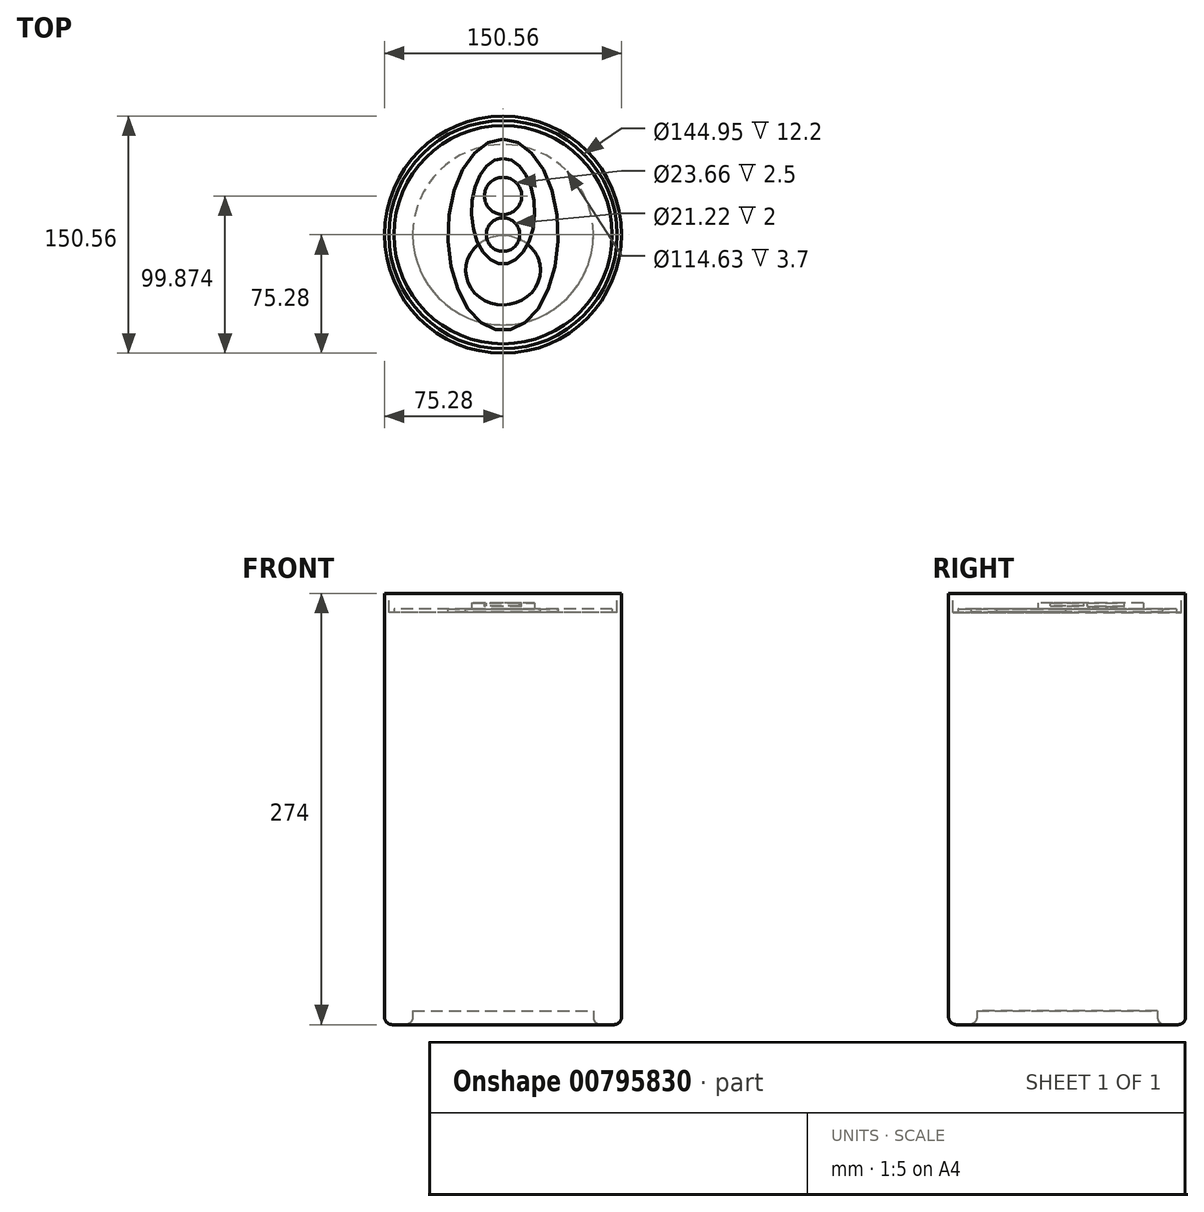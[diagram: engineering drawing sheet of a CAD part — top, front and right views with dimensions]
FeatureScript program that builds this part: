
annotation { "Feature Type Name" : "Feature", "Feature Type Description" : "" }
export const myFeature = defineFeature(function(context is Context, id is Id, definition is map)
    precondition{}
    {
        {
            var Q0;
            Q0=qCreatedBy(makeId("Top.planeOp"),FACE);
            var sketch = newSketch(context, id + "F0", { "sketchPlane" : qUnion([Q0])});
            skCircle(sketch, "E0", {"center": v(0, 0) * mm, "radius": 75.28 * mm});
            skSolve(sketch);
        }
        {
            var Q0;
            Q0=makeQuery(id+"F0.imprint","IMPRINT",FACE,{"disambiguationData":[TD([[makeQuery(id+"F0.imprint","IMPRINT",EDGE,{"derivedFrom":sQuery(id+"F0.wireOp",EDGE,"E0")}),1.0]])]});
            extrude(context, id + "F1", {"entities" : qUnion([Q0]), "depth" : 104 * mm, "offsetDistance" : 25 * mm});
        }
        {
            var Q0;
            Q0=makeQuery(id+"F1.opExtrude","CAP_FACE",FACE,{"disambiguationData":[OSD([sQuery(id+"F0.wireOp",EDGE,"E0")])],"isStart":true});
            extrude(context, id + "F2", {"entities" : qUnion([Q0]), "operationType" : NewBodyOperationType.ADD, "depth" : 131 * mm, "offsetDistance" : 25 * mm});
        }
        {
            var Q0;
            Q0=makeQuery(id+"F1.opExtrude","CAP_FACE",FACE,{"disambiguationData":[OSD([sQuery(id+"F0.wireOp",EDGE,"E0")])],"isStart":false});
            extrude(context, id + "F3", {"entities" : qUnion([Q0]), "operationType" : NewBodyOperationType.ADD, "depth" : 39 * mm, "offsetDistance" : 25 * mm});
        }
        {
            var Q0;
            Q0=makeQuery(id+"F3.opExtrude","CAP_FACE",FACE,{"disambiguationData":[OSD([sQuery(id+"F0.wireOp",EDGE,"E0")])],"isStart":false});
            var sketch = newSketch(context, id + "F4", { "sketchPlane" : qUnion([Q0])});
            skCircle(sketch, "E1", {"center": v(0, 0) * mm, "radius": 72.48 * mm});
            skSolve(sketch);
        }
        {
            var Q0;
            Q0 = qSketchRegion(id + "F4", true);
            extrude(context, id + "F5", {"entities" : qUnion([Q0]), "operationType" : NewBodyOperationType.REMOVE, "oppositeDirection" : true, "depth" : 12.2 * mm, "offsetDistance" : 25 * mm});
        }
        {
            var Q0;
            Q0=makeQuery(id+"F5.boolean.opBoolean","COPY",FACE,{"derivedFrom":makeQuery(id+"F5.opExtrude","CAP_FACE",FACE,{"disambiguationData":[OSD([sQuery(id+"F4.wireOp",EDGE,"E1")])],"isStart":false})});
            var sketch = newSketch(context, id + "F6", { "sketchPlane" : qUnion([Q0])});
            skCircle(sketch, "E2", {"center": v(0, 0) * mm, "radius": 69.32 * mm});
            skSolve(sketch);
        }
        {
            var Q0;
            Q0 = qSketchRegion(id + "F6", true);
            extrude(context, id + "F7", {"entities" : qUnion([Q0]), "operationType" : NewBodyOperationType.ADD, "depth" : 2.3 * mm, "offsetDistance" : 25 * mm});
        }
        {
            var Q0;
            Q0=makeQuery(id+"F7.opExtrude","CAP_FACE",FACE,{"disambiguationData":[OSD([sQuery(id+"F6.wireOp",EDGE,"E2")])],"isStart":false});
            var sketch = newSketch(context, id + "F8", { "sketchPlane" : qUnion([Q0])});
            skSolve(sketch);
        }
        {
            var Q0;
            Q0=makeQuery(id+"F8.imprint","IMPRINT",FACE,{"disambiguationData":[TD([[makeQuery(id+"F8.imprint","IMPRINT",EDGE,{"derivedFrom":makeQuery(id+"F7.opExtrude","CAP_EDGE",EDGE,{"disambiguationData":[OSD([sQuery(id+"F6.wireOp",EDGE,"E2")])],"isStart":false})}),1.0]])]});
            var sketch = newSketch(context, id + "F9", { "sketchPlane" : qUnion([Q0])});
            skEllipse(sketch, "E3", {"center": v(0, 0) * mm, "majorRadius": 60.7 * mm, "minorRadius": 35.1 * mm, "majorAxis": v(0, 1)});
            skSolve(sketch);
        }
        {
            var Q0;
            Q0=makeQuery(id+"F9.imprint","IMPRINT",FACE,{"disambiguationData":[TD([[makeQuery(id+"F9.imprint","IMPRINT",EDGE,{"derivedFrom":sQuery(id+"F9.wireOp",EDGE,"E3")}),1.0]])]});
            extrude(context, id + "F10", {"entities" : qUnion([Q0]), "operationType" : NewBodyOperationType.REMOVE, "oppositeDirection" : true, "depth" : 2.1 * mm, "offsetDistance" : 25 * mm});
        }
        {
            var Q0;
            Q0=makeQuery(id+"F8.imprint","IMPRINT",FACE,{"disambiguationData":[TD([[makeQuery(id+"F8.imprint","IMPRINT",EDGE,{"derivedFrom":makeQuery(id+"F7.opExtrude","CAP_EDGE",EDGE,{"disambiguationData":[OSD([sQuery(id+"F6.wireOp",EDGE,"E2")])],"isStart":false})}),1.0]])]});
            var sketch = newSketch(context, id + "F11", { "sketchPlane" : qUnion([Q0])});
            skEllipse(sketch, "E4", {"center": v(0, 14.93) * mm, "majorRadius": 33.55 * mm, "minorRadius": 20.05 * mm, "majorAxis": v(0, 1)});
            skSolve(sketch);
        }
        {
            var Q0;
            Q0=makeQuery(id+"F11.imprint","IMPRINT",FACE,{"disambiguationData":[TD([[makeQuery(id+"F11.imprint","IMPRINT",EDGE,{"derivedFrom":sQuery(id+"F11.wireOp",EDGE,"E4")}),1.0]])]});
            extrude(context, id + "F12", {"entities" : qUnion([Q0]), "depth" : 3.9 * mm, "offsetDistance" : 25 * mm});
        }
        {
            var Q0;
            Q0=makeQuery(id+"F8.imprint","IMPRINT",FACE,{"disambiguationData":[TD([[makeQuery(id+"F8.imprint","IMPRINT",EDGE,{"derivedFrom":makeQuery(id+"F7.opExtrude","CAP_EDGE",EDGE,{"disambiguationData":[OSD([sQuery(id+"F6.wireOp",EDGE,"E2")])],"isStart":false})}),1.0]])]});
            var sketch = newSketch(context, id + "F13", { "sketchPlane" : qUnion([Q0])});
            skEllipse(sketch, "E5", {"center": v(0, -22.6) * mm, "majorRadius": 23.74 * mm, "minorRadius": 21.98 * mm, "majorAxis": v(1, 0)});
            skSolve(sketch);
        }
        {
            var Q0;
            Q0 = qSketchRegion(id + "F13", true);
            extrude(context, id + "F14", {"entities" : qUnion([Q0]), "operationType" : NewBodyOperationType.ADD, "oppositeDirection" : true, "depth" : 2.4 * mm, "offsetDistance" : 25 * mm});
        }
        {
            var Q0;
            Q0=makeQuery(id+"F12.opExtrude","CAP_FACE",FACE,{"disambiguationData":[OSD([sQuery(id+"F11.wireOp",EDGE,"E4")])],"isStart":false});
            var sketch = newSketch(context, id + "F15", { "sketchPlane" : qUnion([Q0])});
            skCircle(sketch, "E6", {"center": v(0, 24.6) * mm, "radius": 11.83 * mm});
            skCircle(sketch, "E7", {"center": v(0, 0) * mm, "radius": 10.61 * mm});
            skSolve(sketch);
        }
        {
            var Q0;
            Q0=makeQuery(id+"F15.imprint","IMPRINT",FACE,{"disambiguationData":[TD([[makeQuery(id+"F15.imprint","IMPRINT",EDGE,{"derivedFrom":sQuery(id+"F15.wireOp",EDGE,"E6")}),1.0]])]});
            extrude(context, id + "F16", {"entities" : qUnion([Q0]), "operationType" : NewBodyOperationType.REMOVE, "oppositeDirection" : true, "depth" : 2.5 * mm, "offsetDistance" : 25 * mm});
        }
        {
            var Q0;
            Q0=makeQuery(id+"F15.imprint","IMPRINT",FACE,{"disambiguationData":[TD([[makeQuery(id+"F15.imprint","IMPRINT",EDGE,{"derivedFrom":sQuery(id+"F15.wireOp",EDGE,"E7")}),1.0]])]});
            extrude(context, id + "F17", {"entities" : qUnion([Q0]), "operationType" : NewBodyOperationType.REMOVE, "oppositeDirection" : true, "depth" : 2 * mm, "offsetDistance" : 25 * mm});
        }
        {
            var Q0;
            Q0=makeQuery(id+"F2.opExtrude","CAP_FACE",FACE,{"disambiguationData":[OSD([sQuery(id+"F0.wireOp",EDGE,"E0")])],"isStart":false});
            var sketch = newSketch(context, id + "F18", { "sketchPlane" : qUnion([Q0])});
            skCircle(sketch, "E8", {"center": v(0, 0) * mm, "radius": 57.31 * mm});
            skSolve(sketch);
        }
        {
            var Q0;
            Q0=makeQuery(id+"F18.imprint","IMPRINT",FACE,{"disambiguationData":[TD([[makeQuery(id+"F18.imprint","IMPRINT",EDGE,{"derivedFrom":sQuery(id+"F18.wireOp",EDGE,"E8")}),1.0]])]});
            extrude(context, id + "F19", {"entities" : qUnion([Q0]), "operationType" : NewBodyOperationType.REMOVE, "oppositeDirection" : true, "depth" : 8.7 * mm, "offsetDistance" : 25 * mm});
        }
        {
            var Q0;
            Q0=makeQuery(id+"F2.opExtrude","CAP_FACE",FACE,{"disambiguationData":[OSD([sQuery(id+"F0.wireOp",EDGE,"E0")])],"isStart":false});
            fillet(context, id + "F20", {"entities" : qUnion([Q0]), "radius" : 5 * mm, "tangentPropagation" : true, "allowEdgeOverflow" : false});
        }
    });
